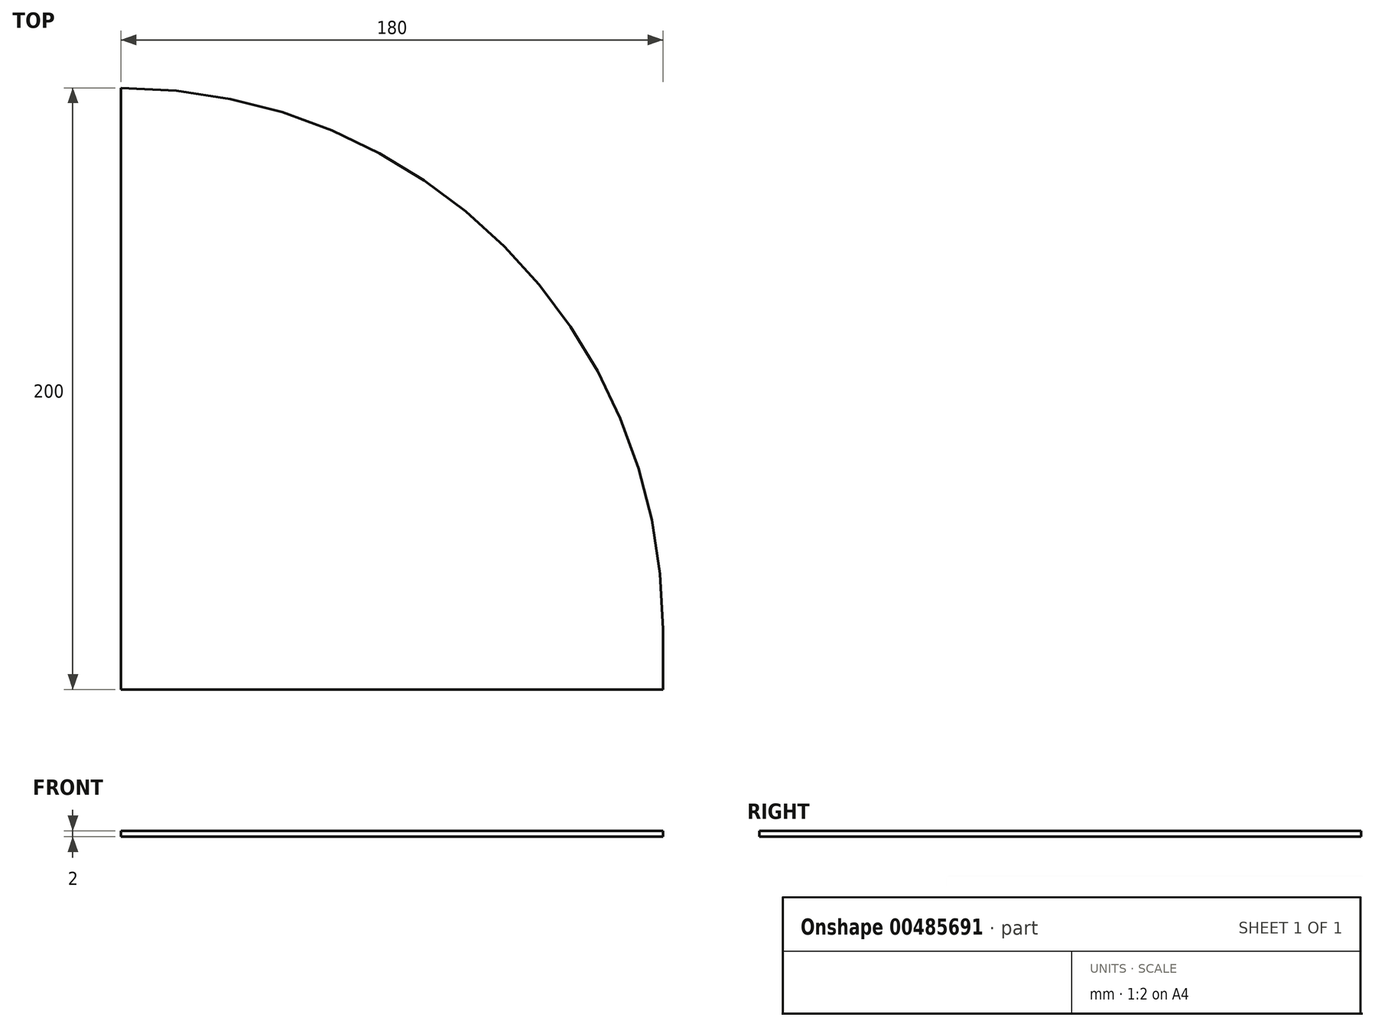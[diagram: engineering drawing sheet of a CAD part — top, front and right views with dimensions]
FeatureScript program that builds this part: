
annotation { "Feature Type Name" : "Feature", "Feature Type Description" : "" }
export const myFeature = defineFeature(function(context is Context, id is Id, definition is map)
    precondition{}
    {
        {
            var Q0;
            Q0=qCreatedBy(makeId("Top.planeOp"),FACE);
            var sketch = newSketch(context, id + "F0", { "sketchPlane" : qUnion([Q0])});
            skLineSegment(sketch, "E0", {"start": v(0, 200) * mm, "end": v(0, 0) * mm});
            skLineSegment(sketch, "E1", {"start": v(0, 0) * mm, "end": v(180, 0) * mm});
            skLineSegment(sketch, "E2", {"start": v(0, 200) * mm, "end": v(0, 200) * mm});
            skLineSegment(sketch, "E3", {"start": v(180, 20) * mm, "end": v(180, 0) * mm});
            skPoint(sketch, "E4.visualSharp", {"position": v(180, 200) * mm});
            skArc(sketch, "E4.filletArc", {"start": v(180, 20) * mm, "mid": v(127.28, 147.28) * mm, "end": v(0, 200) * mm});
            skSolve(sketch);
        }
        {
            var Q0;
            Q0 = qSketchRegion(id + "F0", true);
            extrude(context, id + "F1", {"entities" : qUnion([Q0]), "depth" : 2 * mm});
        }
    });
